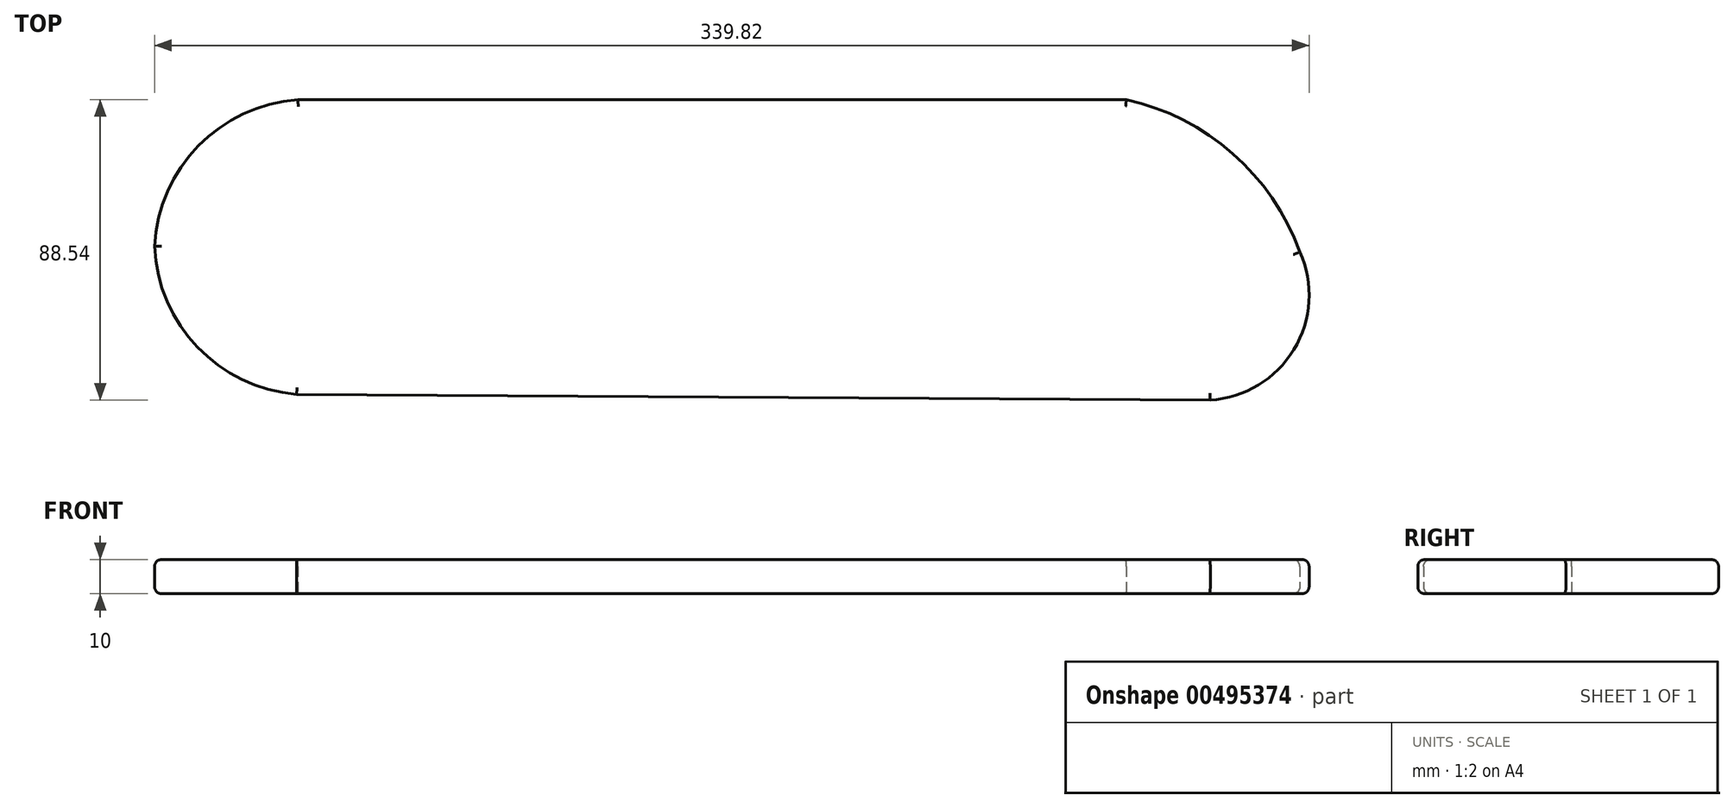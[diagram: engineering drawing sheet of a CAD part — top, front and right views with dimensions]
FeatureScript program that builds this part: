
annotation { "Feature Type Name" : "Feature", "Feature Type Description" : "" }
export const myFeature = defineFeature(function(context is Context, id is Id, definition is map)
    precondition{}
    {
        {
            var Q0;
            Q0=qCreatedBy(makeId("Top.planeOp"),FACE);
            var sketch = newSketch(context, id + "F0", { "sketchPlane" : qUnion([Q0])});
            skLineSegment(sketch, "E0.bottom", {"start": v(-50.18, 43.13) * mm, "end": v(193.66, 43.13) * mm});
            skLineSegment(sketch, "E0.left", {"start": v(-92.43, 0) * mm, "end": v(-92.43, -1.76) * mm});
            skLineSegment(sketch, "E0.right", {"start": v(244.72, -1.56) * mm, "end": v(244.72, -1.76) * mm});
            skPoint(sketch, "E1.endSnap0", {"position": v(-92.43, -1.76) * mm});
            skPoint(sketch, "E2.orphan", {"position": v(-92.43, 43.13) * mm});
            skPoint(sketch, "E0.top.start.orphan", {"position": v(-92.43, -46.66) * mm});
            skArc(sketch, "E3", {"start": v(244.72, -1.76) * mm, "mid": v(224.95, 27.24) * mm, "end": v(193.66, 43.13) * mm});
            skArc(sketch, "E4", {"start": v(218.36, -45.41) * mm, "mid": v(242.98, -30.5) * mm, "end": v(244.72, -1.76) * mm});
            skPoint(sketch, "E5.orphan", {"position": v(244.72, 43.13) * mm});
            skPoint(sketch, "E6.orphan", {"position": v(291.38, -1.76) * mm});
            skLineSegment(sketch, "E7.trimOffspring", {"start": v(244.65, -1.56) * mm, "end": v(244.72, -1.56) * mm, "construction": true});
            skPoint(sketch, "E8.orphan", {"position": v(244.72, -46.66) * mm});
            skLineSegment(sketch, "E9", {"start": v(244.61, -1.47) * mm, "end": v(244.72, -1.56) * mm});
            skArc(sketch, "E10", {"start": v(-50.18, 43.13) * mm, "mid": v(-80.03, 28.9) * mm, "end": v(-92.43, -1.76) * mm});
            skLineSegment(sketch, "E11", {"start": v(-92.43, -0.11) * mm, "end": v(-92.38, -0.11) * mm, "construction": true});
            skArc(sketch, "E12.MirrorCS", {"start": v(-50.55, -43.72) * mm, "mid": v(-80.28, -29.24) * mm, "end": v(-92.42, 1.53) * mm});
            skPoint(sketch, "E13.MirrorCS.end.orphan", {"position": v(-92.43, -0.23) * mm});
            skPoint(sketch, "E1.start.orphan", {"position": v(-118.84, 0) * mm});
            skLineSegment(sketch, "E14", {"start": v(218.36, -45.41) * mm, "end": v(-50.55, -43.72) * mm});
            skLineSegment(sketch, "E15", {"start": v(77.4, 43.13) * mm, "end": v(55.62, 25.26) * mm});
            skLineSegment(sketch, "E16", {"start": v(55.62, 25.26) * mm, "end": v(55.62, 35.85) * mm});
            skLineSegment(sketch, "E17", {"start": v(55.62, 35.85) * mm, "end": v(44.44, 35.85) * mm});
            skLineSegment(sketch, "E18", {"start": v(44.44, 35.85) * mm, "end": v(44.44, 0) * mm});
            skLineSegment(sketch, "E19", {"start": v(44.44, 0) * mm, "end": v(55.62, 0) * mm});
            skLineSegment(sketch, "E20", {"start": v(55.62, 0) * mm, "end": v(55.62, 10.54) * mm});
            skLineSegment(sketch, "E21", {"start": v(55.62, 10.54) * mm, "end": v(77.4, -5.34) * mm});
            skLineSegment(sketch, "E22", {"start": v(77.4, -5.34) * mm, "end": v(55.62, -16.53) * mm});
            skLineSegment(sketch, "E23", {"start": v(55.62, -16.53) * mm, "end": v(44.44, -10.64) * mm});
            skLineSegment(sketch, "E24", {"start": v(44.44, -10.64) * mm, "end": v(44.44, -31.83) * mm});
            skLineSegment(sketch, "E25", {"start": v(44.44, -31.83) * mm, "end": v(55.62, -27.12) * mm});
            skLineSegment(sketch, "E26", {"start": v(55.62, -27.12) * mm, "end": v(55.62, -37.12) * mm});
            skLineSegment(sketch, "E27", {"start": v(55.62, -37.12) * mm, "end": v(77.4, -44.53) * mm});
            skSolve(sketch);
        }
        {
            var Q0;
            {var subQ0=sQuery(id+"F0.wireOp",EDGE,"E15");Q0=makeQuery(id+"F0.imprint","IMPRINT",FACE,{"disambiguationData":[TD([[makeQuery(id+"F0.imprint","IMPRINT",EDGE,{"derivedFrom":subQ0}),-1.0]])]});}
            var Q1;
            {var subQ2=sQuery(id+"F0.wireOp",EDGE,"E4");Q1=makeQuery(id+"F0.imprint","IMPRINT",FACE,{"disambiguationData":[TD([[makeQuery(id+"F0.imprint","IMPRINT",EDGE,{"derivedFrom":subQ2}),1.0]])]});}
            extrude(context, id + "F1", {"entities" : qUnion([Q0, Q1]), "depth" : 10 * mm});
        }
        {
            var Q0;
            Q0=makeQuery(id+"F1.opExtrude","CAP_EDGE",EDGE,{"disambiguationData":[OSD([sQuery(id+"F0.wireOp",EDGE,"E12.MirrorCS")])],"isStart":false});
            var Q1;
            Q1=makeQuery(id+"F1.opExtrude","CAP_EDGE",EDGE,{"disambiguationData":[OSD([sQuery(id+"F0.wireOp",EDGE,"E14")])],"isStart":false});
            var Q2;
            Q2=makeQuery(id+"F1.opExtrude","CAP_EDGE",EDGE,{"disambiguationData":[OSD([sQuery(id+"F0.wireOp",EDGE,"E10")])],"isStart":false});
            var Q3;
            Q3=makeQuery(id+"F1.opExtrude","CAP_EDGE",EDGE,{"disambiguationData":[OSD([sQuery(id+"F0.wireOp",EDGE,"E0.bottom")])],"isStart":false});
            var Q4;
            Q4=makeQuery(id+"F1.opExtrude","CAP_EDGE",EDGE,{"disambiguationData":[OSD([sQuery(id+"F0.wireOp",EDGE,"E4")])],"isStart":false});
            var Q5;
            Q5=makeQuery(id+"F1.opExtrude","CAP_EDGE",EDGE,{"disambiguationData":[OSD([sQuery(id+"F0.wireOp",EDGE,"E3")])],"isStart":false});
            fillet(context, id + "F2", {"entities" : qUnion([Q0, Q1, Q2, Q3, Q4, Q5]), "radius" : 2 * mm, "tangentPropagation" : true, "allowEdgeOverflow" : false});
        }
        {
            var Q0;
            Q0=makeQuery(id+"F1.opExtrude","CAP_EDGE",EDGE,{"disambiguationData":[OSD([sQuery(id+"F0.wireOp",EDGE,"E0.bottom")])],"isStart":true});
            var Q1;
            Q1=makeQuery(id+"F1.opExtrude","CAP_EDGE",EDGE,{"disambiguationData":[OSD([sQuery(id+"F0.wireOp",EDGE,"E12.MirrorCS")])],"isStart":true});
            var Q2;
            Q2=makeQuery(id+"F1.opExtrude","CAP_EDGE",EDGE,{"disambiguationData":[OSD([sQuery(id+"F0.wireOp",EDGE,"E10")])],"isStart":true});
            var Q3;
            Q3=makeQuery(id+"F1.opExtrude","CAP_EDGE",EDGE,{"disambiguationData":[OSD([sQuery(id+"F0.wireOp",EDGE,"E14")])],"isStart":true});
            var Q4;
            Q4=makeQuery(id+"F1.opExtrude","CAP_EDGE",EDGE,{"disambiguationData":[OSD([sQuery(id+"F0.wireOp",EDGE,"E4")])],"isStart":true});
            var Q5;
            Q5=makeQuery(id+"F1.opExtrude","CAP_EDGE",EDGE,{"disambiguationData":[OSD([sQuery(id+"F0.wireOp",EDGE,"E3")])],"isStart":true});
            fillet(context, id + "F3", {"entities" : qUnion([Q0, Q1, Q2, Q3, Q4, Q5]), "radius" : 2 * mm, "tangentPropagation" : true, "allowEdgeOverflow" : false});
        }
    });
